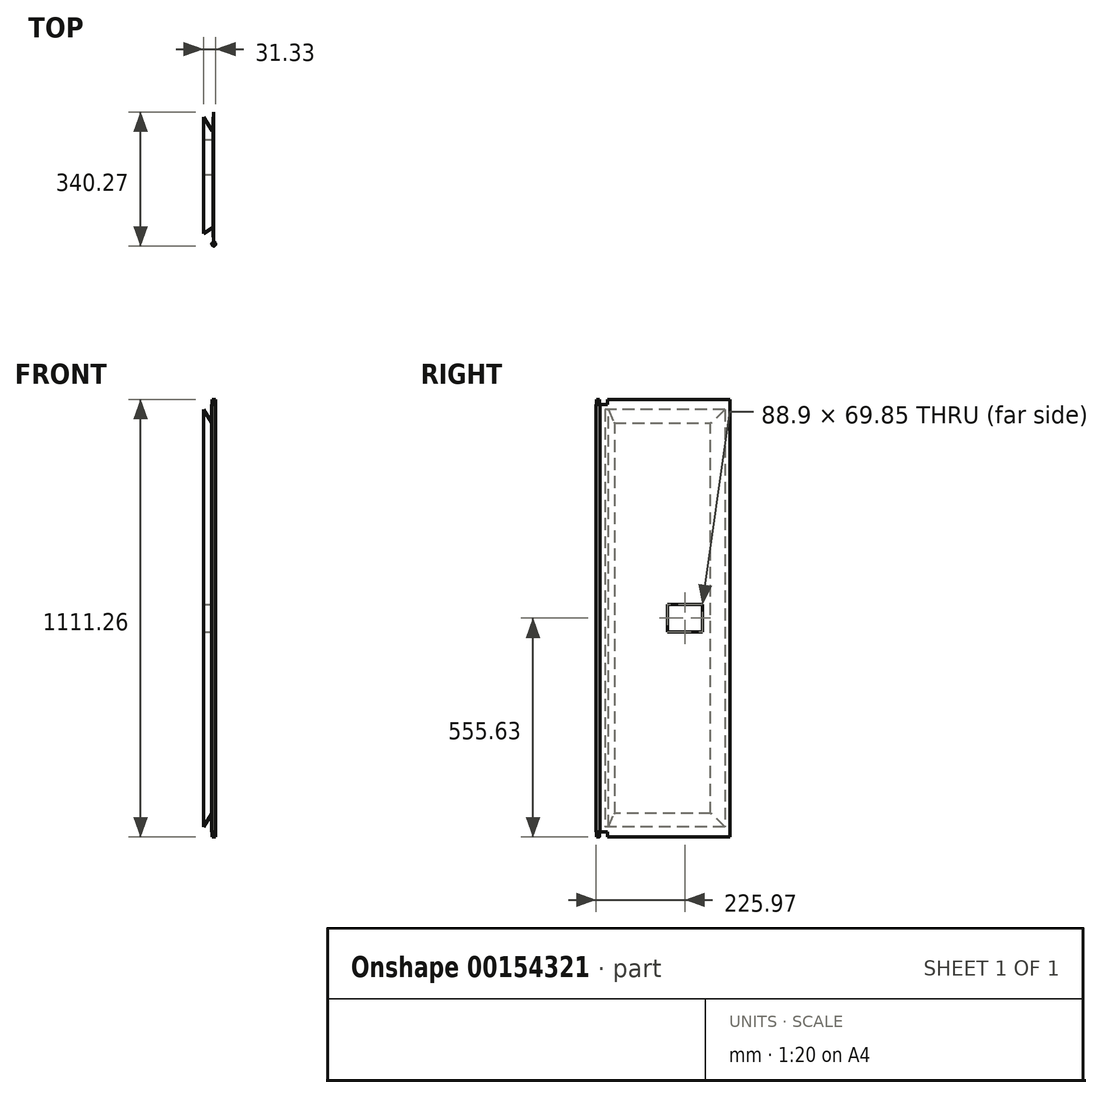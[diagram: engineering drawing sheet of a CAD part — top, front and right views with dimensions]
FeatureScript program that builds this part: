
annotation { "Feature Type Name" : "Feature", "Feature Type Description" : "" }
export const myFeature = defineFeature(function(context is Context, id is Id, definition is map)
    precondition{}
    {
        {
            var Q0;
            Q0=qCreatedBy(makeId("Right.planeOp"),FACE);
            var sketch = newSketch(context, id + "F0", { "sketchPlane" : qUnion([Q0])});
            skLineSegment(sketch, "E0.bottom", {"start": v(-146.05, 555.62) * mm, "end": v(165.1, 555.62) * mm});
            skLineSegment(sketch, "E0.left", {"start": v(-165.1, 542.92) * mm, "end": v(-165.1, -542.92) * mm});
            skLineSegment(sketch, "E0.right", {"start": v(165.1, 555.62) * mm, "end": v(165.1, -555.62) * mm});
            skPoint(sketch, "E0.middle", {"position": v(0, 0) * mm});
            skLineSegment(sketch, "E1", {"start": v(-165.1, 542.92) * mm, "end": v(-146.05, 542.92) * mm});
            skLineSegment(sketch, "E2", {"start": v(-146.05, 542.92) * mm, "end": v(-146.05, 555.62) * mm});
            skLineSegment(sketch, "E3", {"start": v(165.1, -555.62) * mm, "end": v(-146.05, -555.62) * mm});
            skLineSegment(sketch, "E4", {"start": v(-146.05, -555.62) * mm, "end": v(-146.05, -542.92) * mm});
            skLineSegment(sketch, "E5", {"start": v(-146.05, -542.92) * mm, "end": v(-165.1, -542.92) * mm});
            skLineSegment(sketch, "E6", {"start": v(-165.1, 0) * mm, "end": v(165.1, 0) * mm});
            skSolve(sketch);
        }
        {
            var Q0;
            Q0=qSketchRegion(id+"F0",true);
            extrude(context, id + "F1", {"entities" : qUnion([Q0]), "oppositeDirection" : true, "depth" : 0.89 * mm});
        }
        {
            var Q0;
            Q0=makeQuery(id+"F1.opExtrude","CAP_FACE",FACE,{"disambiguationData":[OSD([sQuery(id+"F0.wireOp",EDGE,"E0.bottom"),sQuery(id+"F0.wireOp",EDGE,"E0.top"),sQuery(id+"F0.wireOp",EDGE,"E0.left"),sQuery(id+"F0.wireOp",EDGE,"E0.right")])],"isStart":false});
            var sketch = newSketch(context, id + "F2", { "sketchPlane" : qUnion([Q0])});
            skLineSegment(sketch, "E7.bottom", {"start": v(-152.4, 530.23) * mm, "end": v(152.4, 530.23) * mm});
            skLineSegment(sketch, "E7.top", {"start": v(-152.4, -530.23) * mm, "end": v(152.4, -530.23) * mm});
            skLineSegment(sketch, "E7.left", {"start": v(-152.4, 530.23) * mm, "end": v(-152.4, -530.23) * mm});
            skLineSegment(sketch, "E7.right", {"start": v(152.4, 530.23) * mm, "end": v(152.4, -530.23) * mm});
            skPoint(sketch, "E7.middle", {"position": v(0, 0) * mm});
            skSolve(sketch);
        }
        {
            var Q0;
            Q0=qSketchRegion(id+"F2",true);
            extrude(context, id + "F3", {"entities" : qUnion([Q0]), "operationType" : NewBodyOperationType.ADD, "depth" : 25.4 * mm});
        }
        {
            var Q0;
            Q0=makeQuery(id+"F3.opExtrude","SWEPT_FACE",FACE,{"disambiguationData":[OSD([sQuery(id+"F2.wireOp",EDGE,"E7.left")])]});
            var sketch = newSketch(context, id + "F4", { "sketchPlane" : qUnion([Q0])});
            skLineSegment(sketch, "E8", {"start": v(26.29, 530.23) * mm, "end": v(26.29, -530.22) * mm});
            skLineSegment(sketch, "E9", {"start": v(26.29, 530.23) * mm, "end": v(2.13, 492.91) * mm});
            skLineSegment(sketch, "E10", {"start": v(2.13, 530.23) * mm, "end": v(2.13, -530.23) * mm});
            skLineSegment(sketch, "E11", {"start": v(26.29, -530.23) * mm, "end": v(2.13, -492.91) * mm});
            skSolve(sketch);
        }
        {
            var Q0;
            {var subQ3=sQuery(id+"F4.wireOp",EDGE,"E11");Q0=makeQuery(id+"F4.imprint","IMPRINT",FACE,{"disambiguationData":[TD([[makeQuery(id+"F4.imprint","IMPRINT",EDGE,{"derivedFrom":subQ3}),1.0]])]});}
            var Q1;
            {var subQ0=sQuery(id+"F4.wireOp",EDGE,"E9");Q1=makeQuery(id+"F4.imprint","IMPRINT",FACE,{"disambiguationData":[TD([[makeQuery(id+"F4.imprint","IMPRINT",EDGE,{"derivedFrom":subQ0}),-1.0]])]});}
            extrude(context, id + "F5", {"entities" : qUnion([Q0, Q1]), "operationType" : NewBodyOperationType.REMOVE, "endBound" : BoundingType.THROUGH_ALL, "oppositeDirection" : true, "depth" : 25.4 * mm});
        }
        {
            var Q0;
            {var subQ0=sQuery(id+"F4.wireOp",EDGE,"E10");var subQ2=sQuery(id+"F2.wireOp",EDGE,"E7.bottom");Q0=makeQuery(id+"F5.boolean.opBoolean","SPLIT",FACE,{"disambiguationData":[TD([makeQuery(id+"F5.opExtrude","SWEPT_FACE",FACE,{"disambiguationData":[OSD([subQ0]),TDD([makeQuery(id+"F4.imprint","IMPRINT",EDGE,{"disambiguationData":[TD([[makeQuery(id+"F4.imprint","INTERSECT",VERTEX,{"derivedFrom":[sQuery(id+"F4.wireOp",EDGE,"E9"),subQ0]}),1.0]])],"derivedFrom":subQ0})])]})])],"derivedFrom":makeQuery(id+"F3.opExtrude","SWEPT_FACE",FACE,{"disambiguationData":[OSD([subQ2])]})});}
            var sketch = newSketch(context, id + "F6", { "sketchPlane" : qUnion([Q0])});
            skLineSegment(sketch, "E12", {"start": v(-26.29, 152.4) * mm, "end": v(-2.13, 115.09) * mm});
            skLineSegment(sketch, "E13", {"start": v(-26.29, 152.4) * mm, "end": v(-2.13, 152.4) * mm});
            skLineSegment(sketch, "E14", {"start": v(-2.13, 115.09) * mm, "end": v(-2.13, 152.4) * mm});
            skLineSegment(sketch, "E15", {"start": v(-2.13, -127.55) * mm, "end": v(-2.13, -152.4) * mm});
            skLineSegment(sketch, "E16", {"start": v(-2.13, -152.4) * mm, "end": v(-38.99, -152.4) * mm});
            skLineSegment(sketch, "E17", {"start": v(-38.99, -152.4) * mm, "end": v(-2.13, -127.55) * mm});
            skSolve(sketch);
        }
        {
            var Q0;
            Q0=makeQuery(id+"F6.imprint","IMPRINT",FACE,{"disambiguationData":[TD([[makeQuery(id+"F6.imprint","IMPRINT",EDGE,{"derivedFrom":sQuery(id+"F6.wireOp",EDGE,"E15")}),1.0]])]});
            var Q1;
            Q1=makeQuery(id+"F6.imprint","IMPRINT",FACE,{"disambiguationData":[TD([[makeQuery(id+"F6.imprint","IMPRINT",EDGE,{"derivedFrom":sQuery(id+"F6.wireOp",EDGE,"E12")}),1.0]])]});
            extrude(context, id + "F7", {"entities" : qUnion([Q0, Q1]), "operationType" : NewBodyOperationType.REMOVE, "endBound" : BoundingType.THROUGH_ALL, "oppositeDirection" : true, "depth" : 25.4 * mm});
        }
        {
            var Q0;
            Q0=makeQuery(id+"F7.boolean.opBoolean","COPY",EDGE,{"derivedFrom":makeQuery(id+"F7.opExtrude","SWEPT_EDGE",EDGE,{"disambiguationData":[OSD([sQuery(id+"F6.wireOp",EDGE,"9kJs9u86-Rynm-MJaU-KLCn-ISIbLXFeB2s4"),sQuery(id+"F6.wireOp",EDGE,"E12")])]})});
            var Q1;
            Q1=makeQuery(id+"F5.boolean.opBoolean","COPY",EDGE,{"derivedFrom":makeQuery(id+"F5.opExtrude","SWEPT_EDGE",EDGE,{"disambiguationData":[OSD([sQuery(id+"F4.wireOp",EDGE,"E9"),sQuery(id+"F4.wireOp",EDGE,"E10")])]})});
            var Q2;
            Q2=makeQuery(id+"F7.boolean.opBoolean","COPY",EDGE,{"derivedFrom":makeQuery(id+"F7.opExtrude","SWEPT_EDGE",EDGE,{"disambiguationData":[OSD([sQuery(id+"F6.wireOp",EDGE,"9kJs9u86-Rynm-MJaU-KLCn-ISIbLXFeB2s4"),sQuery(id+"F6.wireOp",EDGE,"ySAFRI99-aNW5-Edny-cf38-flcK1iuSa7Xp")])]})});
            var Q3;
            Q3=makeQuery(id+"F5.boolean.opBoolean","COPY",EDGE,{"derivedFrom":makeQuery(id+"F5.opExtrude","SWEPT_EDGE",EDGE,{"disambiguationData":[OSD([sQuery(id+"F4.wireOp",EDGE,"E10"),sQuery(id+"F4.wireOp",EDGE,"E11")])]})});
            fillet(context, id + "F8", {"entities" : qUnion([Q0, Q1, Q2, Q3]), "radius" : 1.27 * mm, "tangentPropagation" : true, "allowEdgeOverflow" : false});
        }
        {
            var Q0;
            Q0=makeQuery(id+"F1.opExtrude","CAP_FACE",FACE,{"disambiguationData":[OSD([sQuery(id+"F0.wireOp",EDGE,"E0.bottom"),sQuery(id+"F0.wireOp",EDGE,"E0.top"),sQuery(id+"F0.wireOp",EDGE,"E0.left"),sQuery(id+"F0.wireOp",EDGE,"E0.right")])],"isStart":true});
            var sketch = newSketch(context, id + "F9", { "sketchPlane" : qUnion([Q0])});
            skLineSegment(sketch, "E18", {"start": v(-165.1, 0) * mm, "end": v(165.1, 0) * mm});
            skLineSegment(sketch, "E19.bottom", {"start": v(6.35, 34.93) * mm, "end": v(95.25, 34.93) * mm});
            skLineSegment(sketch, "E19.top", {"start": v(6.35, -34.92) * mm, "end": v(95.25, -34.92) * mm});
            skLineSegment(sketch, "E19.left", {"start": v(6.35, 34.93) * mm, "end": v(6.35, -34.92) * mm});
            skLineSegment(sketch, "E19.right", {"start": v(95.25, 34.93) * mm, "end": v(95.25, -34.92) * mm});
            skPoint(sketch, "E19.middle", {"position": v(50.8, 0) * mm});
            skSolve(sketch);
        }
        {
            var Q0;
            Q0=qSketchRegion(id+"F9",true);
            extrude(context, id + "F10", {"entities" : qUnion([Q0]), "operationType" : NewBodyOperationType.REMOVE, "endBound" : BoundingType.THROUGH_ALL, "oppositeDirection" : true, "depth" : 25.4 * mm});
        }
        {
            var Q0;
            Q0=qCreatedBy(makeId("Top.planeOp"),FACE);
            var sketch = newSketch(context, id + "F11", { "sketchPlane" : qUnion([Q0])});
            skCircle(sketch, "E20", {"center": v(0, -170.14) * mm, "radius": 5.04 * mm});
            skCircle(sketch, "E21", {"center": v(0, -170.14) * mm, "radius": 3.97 * mm});
            skSolve(sketch);
        }
        {
            var Q0;
            Q0=qSketchRegion(id+"F11",true);
            var Q1;
            Q1=makeQuery(id+"F3.boolean.opBoolean","MERGE",FACE,{"derivedFrom":[makeQuery(id+"F1.opExtrude","SWEPT_FACE",FACE,{"disambiguationData":[OSD([sQuery(id+"F0.wireOp",EDGE,"E1")])]}),makeQuery(id+"F3.opExtrude","SWEPT_FACE",FACE,{"disambiguationData":[OSD([sQuery(id+"F2.wireOp",EDGE,"E7.bottom")])]})]});
            var Q2;
            Q2=makeQuery(id+"F3.boolean.opBoolean","MERGE",FACE,{"derivedFrom":[makeQuery(id+"F1.opExtrude","SWEPT_FACE",FACE,{"disambiguationData":[OSD([sQuery(id+"F0.wireOp",EDGE,"E5")])]}),makeQuery(id+"F3.opExtrude","SWEPT_FACE",FACE,{"disambiguationData":[OSD([sQuery(id+"F2.wireOp",EDGE,"E7.top")])]})]});
            extrude(context, id + "F12", {"entities" : qUnion([Q0]), "endBound" : BoundingType.UP_TO_SURFACE, "endBoundEntityFace" : qUnion([Q1]), "depth" : 25.4 * mm, "hasSecondDirection" : true, "secondDirectionBound" : SecondDirectionBoundingType.UP_TO_SURFACE, "secondDirectionOppositeDirection" : true, "secondDirectionBoundEntityFace" : qUnion([Q2]), "secondDirectionDepth" : 25.4 * mm});
        }
        {
            var Q0;
            Q0=qCreatedBy(makeId("Top.planeOp"),FACE);
            var sketch = newSketch(context, id + "F13", { "sketchPlane" : qUnion([Q0])});
            skCircle(sketch, "E22", {"center": v(0, -170.14) * mm, "radius": 3.97 * mm});
            skSolve(sketch);
        }
        {
            var Q0;
            Q0=qSketchRegion(id+"F13",true);
            var Q1;
            Q1=makeQuery(id+"F1.opExtrude","SWEPT_FACE",FACE,{"disambiguationData":[OSD([sQuery(id+"F0.wireOp",EDGE,"E0.bottom")])]});
            var Q2;
            Q2=makeQuery(id+"F1.opExtrude","SWEPT_FACE",FACE,{"disambiguationData":[OSD([sQuery(id+"F0.wireOp",EDGE,"E3")])]});
            extrude(context, id + "F14", {"entities" : qUnion([Q0]), "operationType" : NewBodyOperationType.ADD, "endBound" : BoundingType.UP_TO_SURFACE, "endBoundEntityFace" : qUnion([Q1]), "depth" : 25.4 * mm, "hasSecondDirection" : true, "secondDirectionBound" : SecondDirectionBoundingType.UP_TO_SURFACE, "secondDirectionOppositeDirection" : true, "secondDirectionBoundEntityFace" : qUnion([Q2]), "secondDirectionDepth" : 25.4 * mm});
        }
    });
